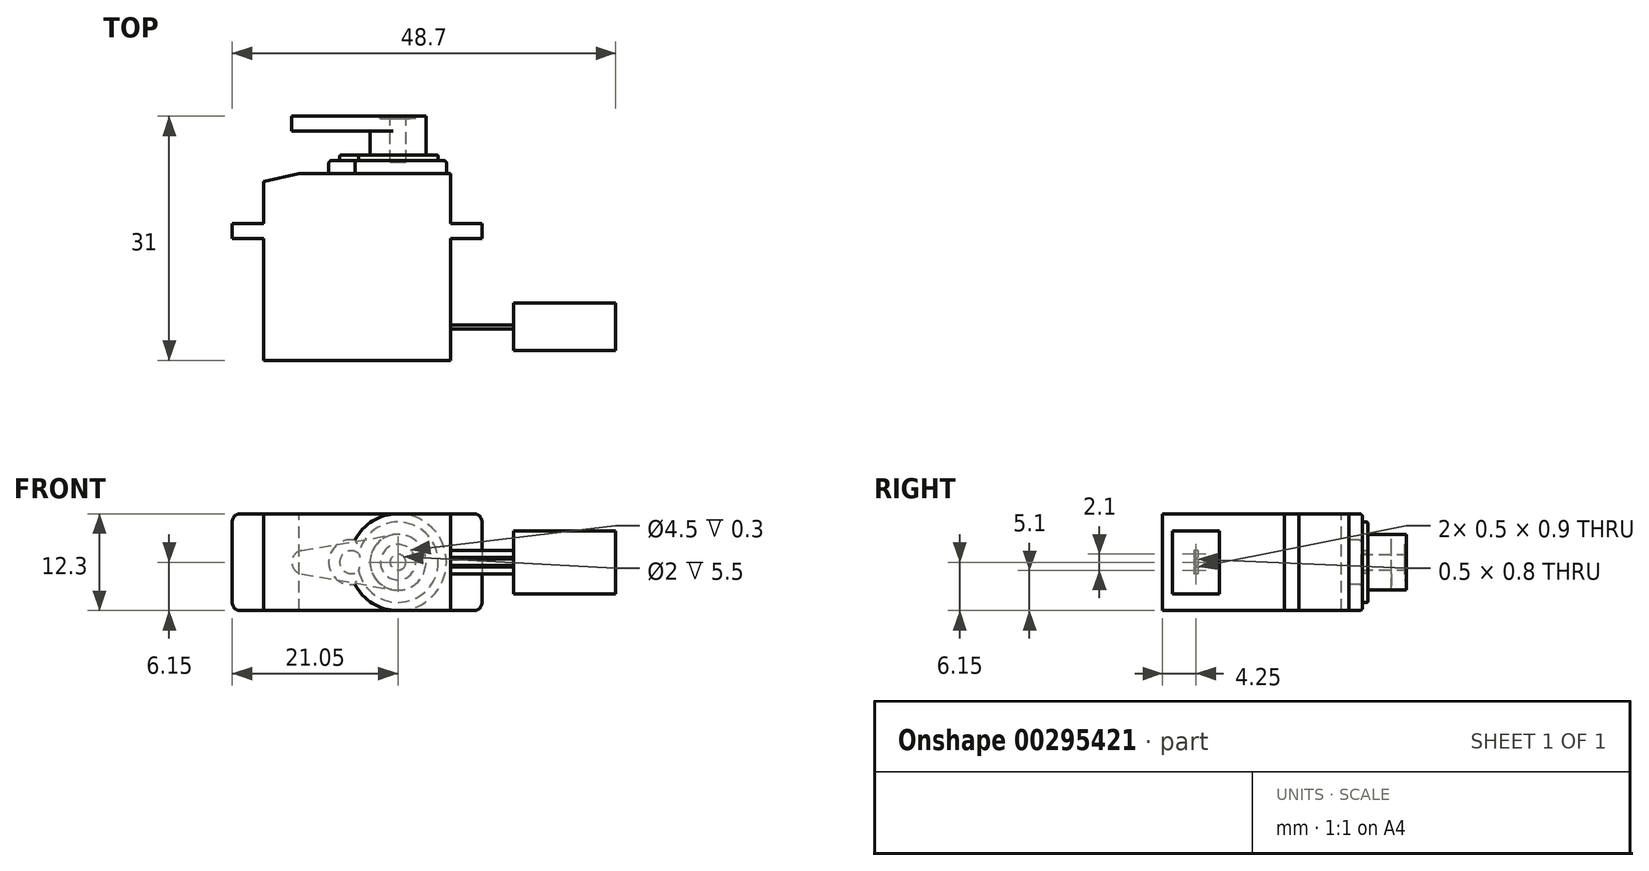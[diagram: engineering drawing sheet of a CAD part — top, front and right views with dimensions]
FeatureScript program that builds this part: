
annotation { "Feature Type Name" : "Feature", "Feature Type Description" : "" }
export const myFeature = defineFeature(function(context is Context, id is Id, definition is map)
    precondition{}
    {
        {
            var Q0;
            Q0=qCreatedBy(makeId("Top.planeOp"),FACE);
            var sketch = newSketch(context, id + "F0", { "sketchPlane" : qUnion([Q0])});
            skLineSegment(sketch, "E0.bottom", {"start": v(11.85, -11.85) * mm, "end": v(-11.85, -11.85) * mm});
            skLineSegment(sketch, "E0.top", {"start": v(11.85, 11.85) * mm, "end": v(-11.85, 11.85) * mm});
            skLineSegment(sketch, "E0.left", {"start": v(11.85, -11.85) * mm, "end": v(11.85, 11.85) * mm});
            skLineSegment(sketch, "E0.right", {"start": v(-11.85, -11.85) * mm, "end": v(-11.85, 11.85) * mm});
            skPoint(sketch, "E0.middle", {"position": v(0, 0) * mm});
            skSolve(sketch);
        }
        {
            var Q0;
            Q0=qSketchRegion(id+"F0",true);
            extrude(context, id + "F1", {"entities" : qUnion([Q0]), "depth" : (12.3 / 2) * mm, "hasSecondDirection" : true, "secondDirectionOppositeDirection" : true, "secondDirectionDepth" : (12.3 / 2) * mm});
        }
        {
            var Q0;
            Q0=makeQuery(id+"F1.opExtrude","SWEPT_FACE",FACE,{"disambiguationData":[OSD([sQuery(id+"F0.wireOp",EDGE,"E0.right")])]});
            var sketch = newSketch(context, id + "F2", { "sketchPlane" : qUnion([Q0])});
            skLineSegment(sketch, "E1", {"start": v(-3.65, 6.15) * mm, "end": v(-3.65, -6.15) * mm});
            skLineSegment(sketch, "E2", {"start": v(-3.65, 6.15) * mm, "end": v(-5.5, 6.15) * mm});
            skLineSegment(sketch, "E3", {"start": v(-5.5, 6.15) * mm, "end": v(-5.5, -6.15) * mm});
            skLineSegment(sketch, "E4", {"start": v(-5.5, -6.15) * mm, "end": v(-3.65, -6.15) * mm});
            skSolve(sketch);
        }
        {
            var Q0;
            Q0=qSketchRegion(id+"F2",true);
            extrude(context, id + "F3", {"entities" : qUnion([Q0]), "operationType" : NewBodyOperationType.ADD, "depth" : 4 * mm});
        }
        {
            var Q0;
            Q0=makeQuery(id+"F1.opExtrude","SWEPT_BODY",BODY,{"disambiguationData":[OSD([sQuery(id+"F0.wireOp",EDGE,"E0.bottom"),sQuery(id+"F0.wireOp",EDGE,"E0.top"),sQuery(id+"F0.wireOp",EDGE,"E0.left"),sQuery(id+"F0.wireOp",EDGE,"E0.right")])]});
            var Q1;
            Q1=qCreatedBy(makeId("Right.planeOp"),FACE);
            mirror(context, id + "F4", {"operationType" : NewBodyOperationType.ADD, "entities" : qUnion([Q0]), "mirrorPlane" : qUnion([Q1])});
        }
        {
            var Q0;
            {var subQ0=makeQuery(id+"F3.boolean.opBoolean","MERGE",FACE,{"derivedFrom":[makeQuery(id+"F1.opExtrude","CAP_FACE",FACE,{"disambiguationData":[OSD([sQuery(id+"F0.wireOp",EDGE,"E0.bottom"),sQuery(id+"F0.wireOp",EDGE,"E0.top"),sQuery(id+"F0.wireOp",EDGE,"E0.left"),sQuery(id+"F0.wireOp",EDGE,"E0.right")])],"isStart":false}),makeQuery(id+"F3.opExtrude","SWEPT_FACE",FACE,{"disambiguationData":[OSD([sQuery(id+"F2.wireOp",EDGE,"E2")])]})]});Q0=makeQuery(id+"F4.boolean.opBoolean","MERGE",FACE,{"derivedFrom":[subQ0,makeQuery(id+"F4.opPattern","COPY",FACE,{"derivedFrom":subQ0,"instanceName":"1"})]});}
            var sketch = newSketch(context, id + "F5", { "sketchPlane" : qUnion([Q0])});
            skLineSegment(sketch, "E5", {"start": v(-11.85, 10.85) * mm, "end": v(-11.85, 11.85) * mm});
            skLineSegment(sketch, "E6", {"start": v(-11.85, 11.85) * mm, "end": v(-7.35, 11.85) * mm});
            skLineSegment(sketch, "E7", {"start": v(-7.35, 11.85) * mm, "end": v(-11.85, 10.85) * mm});
            skSolve(sketch);
        }
        {
            var Q0;
            Q0=qSketchRegion(id+"F5",true);
            extrude(context, id + "F6", {"entities" : qUnion([Q0]), "operationType" : NewBodyOperationType.REMOVE, "oppositeDirection" : true, "depth" : 25 * mm});
        }
        {
            var Q0;
            Q0=makeQuery(id+"F1.opExtrude","SWEPT_FACE",FACE,{"disambiguationData":[OSD([sQuery(id+"F0.wireOp",EDGE,"E0.top")])]});
            var sketch = newSketch(context, id + "F7", { "sketchPlane" : qUnion([Q0])});
            skArc(sketch, "E8", {"start": v(0.27, 2.8) * mm, "mid": v(-11.35, 0) * mm, "end": v(0.27, -2.8) * mm});
            skLineSegment(sketch, "E9.0", {"start": v(-11.85, 6.15) * mm, "end": v(-11.85, -6.15) * mm, "construction": true});
            skLineSegment(sketch, "E10", {"start": v(-11.35, 9.57) * mm, "end": v(-11.35, -8.85) * mm, "construction": true});
            skArc(sketch, "E11", {"start": v(0.27, -2.8) * mm, "mid": v(3.6, 0) * mm, "end": v(0.27, 2.8) * mm});
            skLineSegment(sketch, "E12", {"start": v(3.6, 8.95) * mm, "end": v(3.6, -8.9) * mm, "construction": true});
            skSolve(sketch);
        }
        {
            var Q0;
            Q0=qSketchRegion(id+"F7",true);
            extrude(context, id + "F8", {"entities" : qUnion([Q0]), "operationType" : NewBodyOperationType.ADD, "depth" : (25.4 - 23.7) * mm});
        }
        {
            var Q0;
            Q0=makeQuery(id+"F8.opExtrude","CAP_FACE",FACE,{"disambiguationData":[OSD([sQuery(id+"F7.wireOp",EDGE,"E8"),sQuery(id+"F7.wireOp",EDGE,"E11")])],"isStart":false});
            var sketch = newSketch(context, id + "F9", { "sketchPlane" : qUnion([Q0])});
            skArc(sketch, "E13.0", {"start": v(0.27, -2.8) * mm, "mid": v(3.6, 0) * mm, "end": v(0.27, 2.8) * mm, "construction": true});
            skArc(sketch, "E14.0", {"start": v(0.27, 2.8) * mm, "mid": v(-11.35, 0) * mm, "end": v(0.27, -2.8) * mm, "construction": true});
            skArc(sketch, "E15", {"start": v(-0.22, -1.08) * mm, "mid": v(2.2, 0) * mm, "end": v(-0.22, 1.08) * mm});
            skArc(sketch, "E16", {"start": v(-0.22, 1.08) * mm, "mid": v(-10.3, 0) * mm, "end": v(-0.22, -1.08) * mm});
            skSolve(sketch);
        }
        {
            var Q0;
            Q0=qSketchRegion(id+"F9",true);
            extrude(context, id + "F10", {"entities" : qUnion([Q0]), "operationType" : NewBodyOperationType.ADD, "depth" : 0.7 * mm});
        }
        {
            var Q0;
            Q0=makeQuery(id+"F4.opPattern","COPY",EDGE,{"derivedFrom":makeQuery(id+"F3.opExtrude","CAP_EDGE",EDGE,{"disambiguationData":[OSD([sQuery(id+"F2.wireOp",EDGE,"E4")])],"isStart":false}),"instanceName":"1"});
            var Q1;
            Q1=makeQuery(id+"F3.opExtrude","CAP_EDGE",EDGE,{"disambiguationData":[OSD([sQuery(id+"F2.wireOp",EDGE,"E4")])],"isStart":false});
            var Q2;
            Q2=makeQuery(id+"F4.opPattern","COPY",EDGE,{"derivedFrom":makeQuery(id+"F3.opExtrude","CAP_EDGE",EDGE,{"disambiguationData":[OSD([sQuery(id+"F2.wireOp",EDGE,"E2")])],"isStart":false}),"instanceName":"1"});
            var Q3;
            Q3=makeQuery(id+"F3.opExtrude","CAP_EDGE",EDGE,{"disambiguationData":[OSD([sQuery(id+"F2.wireOp",EDGE,"E2")])],"isStart":false});
            fillet(context, id + "F11", {"entities" : qUnion([Q0, Q1, Q2, Q3]), "radius" : 1 * mm, "tangentPropagation" : true, "allowEdgeOverflow" : false});
        }
        {
            var Q0;
            Q0=makeQuery(id+"F10.opExtrude","CAP_EDGE",EDGE,{"disambiguationData":[OSD([sQuery(id+"F9.wireOp",EDGE,"E16")])],"isStart":false});
            var Q1;
            Q1=makeQuery(id+"F10.opExtrude","CAP_FACE",FACE,{"disambiguationData":[OSD([sQuery(id+"F9.wireOp",EDGE,"E15"),sQuery(id+"F9.wireOp",EDGE,"E16")])],"isStart":false});
            fillet(context, id + "F12", {"entities" : qUnion([Q0, Q1]), "radius" : 0.2 * mm, "tangentPropagation" : true, "allowEdgeOverflow" : false});
        }
        {
            var Q0;
            Q0=makeQuery(id+"F8.opExtrude","CAP_EDGE",EDGE,{"disambiguationData":[OSD([sQuery(id+"F7.wireOp",EDGE,"E8")])],"isStart":false});
            var Q1;
            Q1=makeQuery(id+"F8.opExtrude","CAP_EDGE",EDGE,{"disambiguationData":[OSD([sQuery(id+"F7.wireOp",EDGE,"E11")])],"isStart":false});
            fillet(context, id + "F13", {"entities" : qUnion([Q0, Q1]), "radius" : 0.4 * mm, "tangentPropagation" : true, "allowEdgeOverflow" : false});
        }
        {
            var Q0;
            {var subQ1=sQuery(id+"F0.wireOp",EDGE,"E0.left");var subQ3=sQuery(id+"F0.wireOp",EDGE,"E0.bottom");Q0=makeQuery(id+"F4.boolean.opBoolean","SPLIT",FACE,{"disambiguationData":[TD([makeQuery(id+"F1.opExtrude","SWEPT_FACE",FACE,{"disambiguationData":[OSD([subQ3])]})])],"derivedFrom":makeQuery(id+"F1.opExtrude","SWEPT_FACE",FACE,{"disambiguationData":[OSD([subQ1])]})});}
            var sketch = newSketch(context, id + "F14", { "sketchPlane" : qUnion([Q0])});
            skLineSegment(sketch, "E17.bottom", {"start": v(-7.35, 1.5) * mm, "end": v(-7.85, 1.5) * mm});
            skLineSegment(sketch, "E17.top", {"start": v(-7.35, -1.5) * mm, "end": v(-7.85, -1.5) * mm});
            skLineSegment(sketch, "E17.left", {"start": v(-7.35, 1.5) * mm, "end": v(-7.35, 0.6) * mm});
            skLineSegment(sketch, "E17.right", {"start": v(-7.85, 1.5) * mm, "end": v(-7.85, 0.6) * mm});
            skPoint(sketch, "E17.middle", {"position": v(-7.6, 0) * mm});
            skLineSegment(sketch, "E18", {"start": v(-7.85, 0.5) * mm, "end": v(-7.35, 0.5) * mm, "construction": true});
            skLineSegment(sketch, "E19", {"start": v(-7.85, 0.6) * mm, "end": v(-7.35, 0.6) * mm});
            skLineSegment(sketch, "E20.MirrorCS", {"start": v(-7.85, 0.4) * mm, "end": v(-7.35, 0.4) * mm});
            skLineSegment(sketch, "E21.MirrorCS", {"start": v(-7.85, -0.6) * mm, "end": v(-7.35, -0.6) * mm});
            skLineSegment(sketch, "E22.MirrorCS", {"start": v(-7.85, -0.4) * mm, "end": v(-7.35, -0.4) * mm});
            skLineSegment(sketch, "E23.trimOffspring", {"start": v(-7.35, 0.4) * mm, "end": v(-7.35, -0.4) * mm});
            skLineSegment(sketch, "E24.trimOffspring", {"start": v(-7.85, 0.4) * mm, "end": v(-7.85, -0.4) * mm});
            skLineSegment(sketch, "E25.trimOffspring", {"start": v(-7.35, -0.6) * mm, "end": v(-7.35, -1.5) * mm});
            skLineSegment(sketch, "E26.trimOffspring", {"start": v(-7.85, -0.6) * mm, "end": v(-7.85, -1.5) * mm});
            skSolve(sketch);
        }
        {
            var Q0;
            Q0=qSketchRegion(id+"F14",true);
            extrude(context, id + "F15", {"entities" : qUnion([Q0]), "operationType" : NewBodyOperationType.ADD, "depth" : 8 * mm});
        }
        {
            var Q0;
            Q0=makeQuery(id+"F10.opExtrude","CAP_FACE",FACE,{"disambiguationData":[OSD([sQuery(id+"F9.wireOp",EDGE,"E15"),sQuery(id+"F9.wireOp",EDGE,"E16")])],"isStart":false});
            var sketch = newSketch(context, id + "F16", { "sketchPlane" : qUnion([Q0])});
            skArc(sketch, "E27.0", {"start": v(-0.22, -1.08) * mm, "mid": v(-10.3, 0) * mm, "end": v(-0.22, 1.08) * mm, "construction": true});
            skCircle(sketch, "E28", {"center": v(-5.2, 0) * mm, "radius": 3.55 * mm});
            skSolve(sketch);
        }
        {
            var Q0;
            Q0=qSketchRegion(id+"F16",true);
            extrude(context, id + "F17", {"entities" : qUnion([Q0]), "operationType" : NewBodyOperationType.ADD, "depth" : 3 * mm});
        }
        {
            var Q0;
            Q0=makeQuery(id+"F17.opExtrude","CAP_FACE",FACE,{"disambiguationData":[OSD([sQuery(id+"F16.wireOp",EDGE,"E28")])],"isStart":false});
            var sketch = newSketch(context, id + "F18", { "sketchPlane" : qUnion([Q0])});
            skArc(sketch, "E29.0", {"start": v(-5.43, -3.54) * mm, "mid": v(-5.2, -3.55) * mm, "end": v(-4.97, -3.54) * mm});
            skLineSegment(sketch, "E30", {"start": v(-23.93, 0) * mm, "end": v(13.53, 0) * mm, "construction": true});
            skArc(sketch, "E31", {"start": v(11.19, -2.5) * mm, "mid": v(13.53, 0) * mm, "end": v(11.19, 2.5) * mm});
            skArc(sketch, "E32", {"start": v(-21.59, 2.5) * mm, "mid": v(-23.93, 0) * mm, "end": v(-21.59, -2.5) * mm});
            skLineSegment(sketch, "E33", {"start": v(-4.97, 3.54) * mm, "end": v(11.19, 2.5) * mm});
            skLineSegment(sketch, "E34", {"start": v(-5.43, 3.54) * mm, "end": v(-21.59, 2.5) * mm});
            skLineSegment(sketch, "E35", {"start": v(-5.43, -3.54) * mm, "end": v(-21.59, -2.5) * mm});
            skLineSegment(sketch, "E36", {"start": v(-4.97, -3.54) * mm, "end": v(11.19, -2.5) * mm});
            skArc(sketch, "E37.trimOffspring", {"start": v(-4.97, 3.54) * mm, "mid": v(-5.2, 3.55) * mm, "end": v(-5.43, 3.54) * mm});
            skSolve(sketch);
        }
        {
            var Q0;
            Q0=qSketchRegion(id+"F18",true);
            extrude(context, id + "F19", {"entities" : qUnion([Q0]), "operationType" : NewBodyOperationType.ADD, "depth" : 1.9 * mm});
        }
        {
            var Q0;
            Q0=makeQuery(id+"F19.opExtrude","CAP_FACE",FACE,{"disambiguationData":[OSD([sQuery(id+"F18.wireOp",EDGE,"E29.0"),sQuery(id+"F18.wireOp",EDGE,"E31"),sQuery(id+"F18.wireOp",EDGE,"E32"),sQuery(id+"F18.wireOp",EDGE,"E33"),sQuery(id+"F18.wireOp",EDGE,"E34"),sQuery(id+"F18.wireOp",EDGE,"E35"),sQuery(id+"F18.wireOp",EDGE,"E36"),sQuery(id+"F18.wireOp",EDGE,"E37.trimOffspring")])],"isStart":false});
            var sketch = newSketch(context, id + "F20", { "sketchPlane" : qUnion([Q0])});
            skCircle(sketch, "E38", {"center": v(-5.2, 0) * mm, "radius": 2.25 * mm});
            skSolve(sketch);
        }
        {
            var Q0;
            Q0=qSketchRegion(id+"F20",true);
            extrude(context, id + "F21", {"entities" : qUnion([Q0]), "operationType" : NewBodyOperationType.REMOVE, "oppositeDirection" : true, "depth" : 0.3 * mm});
        }
        {
            var Q0;
            Q0=makeQuery(id+"F21.boolean.opBoolean","COPY",FACE,{"derivedFrom":makeQuery(id+"F21.opExtrude","CAP_FACE",FACE,{"disambiguationData":[OSD([sQuery(id+"F20.wireOp",EDGE,"E38")])],"isStart":false})});
            var sketch = newSketch(context, id + "F22", { "sketchPlane" : qUnion([Q0])});
            skCircle(sketch, "E39.0", {"center": v(-5.2, 0) * mm, "radius": 2.25 * mm, "construction": true});
            skCircle(sketch, "E40", {"center": v(-5.2, 0) * mm, "radius": 1 * mm});
            skSolve(sketch);
        }
        {
            var Q0;
            Q0=qSketchRegion(id+"F22",true);
            extrude(context, id + "F23", {"entities" : qUnion([Q0]), "operationType" : NewBodyOperationType.REMOVE, "oppositeDirection" : true, "depth" : 5.5 * mm});
        }
        {
            var Q0;
            Q0=makeQuery(id+"F19.opExtrude","CAP_FACE",FACE,{"disambiguationData":[OSD([sQuery(id+"F18.wireOp",EDGE,"E29.0"),sQuery(id+"F18.wireOp",EDGE,"E31"),sQuery(id+"F18.wireOp",EDGE,"E32"),sQuery(id+"F18.wireOp",EDGE,"E33"),sQuery(id+"F18.wireOp",EDGE,"E34"),sQuery(id+"F18.wireOp",EDGE,"E35"),sQuery(id+"F18.wireOp",EDGE,"E36"),sQuery(id+"F18.wireOp",EDGE,"E37.trimOffspring")])],"isStart":false});
            var sketch = newSketch(context, id + "F24", { "sketchPlane" : qUnion([Q0])});
            skArc(sketch, "E41", {"start": v(7.06, -1.48) * mm, "mid": v(8.3, 0) * mm, "end": v(7.06, 1.48) * mm});
            skArc(sketch, "E42", {"start": v(-4.97, -3.54) * mm, "mid": v(-4.78, -3.53) * mm, "end": v(-4.6, -3.5) * mm});
            skLineSegment(sketch, "E43", {"start": v(7.06, 1.48) * mm, "end": v(-4.6, 3.5) * mm});
            skLineSegment(sketch, "E44", {"start": v(7.06, -1.48) * mm, "end": v(-4.6, -3.5) * mm});
            skPoint(sketch, "E45.0.end.orphan", {"position": v(-4.97, -3.54) * mm});
            skPoint(sketch, "E46.0.start.orphan", {"position": v(-4.97, 3.54) * mm});
            skLineSegment(sketch, "E47", {"start": v(-5.2, 6.74) * mm, "end": v(-5.2, -4.93) * mm, "construction": true});
            skArc(sketch, "E48.trimOffspring", {"start": v(-4.6, 3.5) * mm, "mid": v(-4.78, 3.53) * mm, "end": v(-4.97, 3.54) * mm});
            skLineSegment(sketch, "E49.0", {"start": v(-4.97, 3.54) * mm, "end": v(11.19, 2.5) * mm});
            skArc(sketch, "E50.0", {"start": v(11.19, -2.5) * mm, "mid": v(13.53, 0) * mm, "end": v(11.19, 2.5) * mm});
            skLineSegment(sketch, "E51.0", {"start": v(-4.97, -3.54) * mm, "end": v(11.19, -2.5) * mm});
            skArc(sketch, "E52", {"start": v(-4.6, 3.5) * mm, "mid": v(-4.9, 3.54) * mm, "end": v(-5.2, 3.55) * mm});
            skLineSegment(sketch, "E53.0", {"start": v(-5.43, 3.54) * mm, "end": v(-21.59, 2.5) * mm});
            skArc(sketch, "E54.0", {"start": v(-21.59, 2.5) * mm, "mid": v(-23.93, 0) * mm, "end": v(-21.59, -2.5) * mm});
            skLineSegment(sketch, "E55.0", {"start": v(-5.43, -3.54) * mm, "end": v(-21.59, -2.5) * mm});
            skArc(sketch, "E56.trimOffspring", {"start": v(-5.2, -3.55) * mm, "mid": v(-4.9, -3.54) * mm, "end": v(-4.6, -3.5) * mm});
            skArc(sketch, "E57.trimOffspring", {"start": v(-5.43, 3.54) * mm, "mid": v(-8.75, 0) * mm, "end": v(-5.43, -3.54) * mm});
            skSolve(sketch);
        }
        {
            var Q0;
            Q0 = qSketchRegion(id + "F24", true);
            extrude(context, id + "F25", {"entities" : qUnion([Q0]), "operationType" : NewBodyOperationType.REMOVE, "oppositeDirection" : true, "depth" : 2 * mm});
        }
        {
            var Q0;
            Q0=makeQuery(id+"F15.opExtrude","CAP_FACE",FACE,{"disambiguationData":[OSD([sQuery(id+"F14.wireOp",EDGE,"E17.bottom"),sQuery(id+"F14.wireOp",EDGE,"E17.left"),sQuery(id+"F14.wireOp",EDGE,"E17.right"),sQuery(id+"F14.wireOp",EDGE,"E19")])],"isStart":false});
            var sketch = newSketch(context, id + "F26", { "sketchPlane" : qUnion([Q0])});
            skLineSegment(sketch, "E58.0", {"start": v(-7.85, 0.4) * mm, "end": v(-7.35, 0.4) * mm, "construction": true});
            skLineSegment(sketch, "E59.0", {"start": v(-7.35, 0.4) * mm, "end": v(-7.35, -0.4) * mm, "construction": true});
            skLineSegment(sketch, "E60", {"start": v(-7.6, 0.4) * mm, "end": v(-7.6, -0.58) * mm, "construction": true});
            skLineSegment(sketch, "E61", {"start": v(-7.35, 0) * mm, "end": v(-10.6, 0) * mm, "construction": true});
            skPoint(sketch, "E61.endSnap0", {"position": v(-7.35, 0) * mm});
            skLineSegment(sketch, "E62.bottom", {"start": v(-4.6, -4) * mm, "end": v(-10.6, -4) * mm});
            skLineSegment(sketch, "E62.top", {"start": v(-4.6, 4) * mm, "end": v(-10.6, 4) * mm});
            skLineSegment(sketch, "E62.left", {"start": v(-4.6, -4) * mm, "end": v(-4.6, 4) * mm});
            skLineSegment(sketch, "E62.right", {"start": v(-10.6, -4) * mm, "end": v(-10.6, 4) * mm});
            skPoint(sketch, "E62.middle", {"position": v(-7.6, 0) * mm});
            skSolve(sketch);
        }
        {
            var Q0;
            Q0 = qSketchRegion(id + "F26", true);
            extrude(context, id + "F27", {"entities" : qUnion([Q0]), "operationType" : NewBodyOperationType.ADD, "depth" : 13 * mm});
        }
    });
